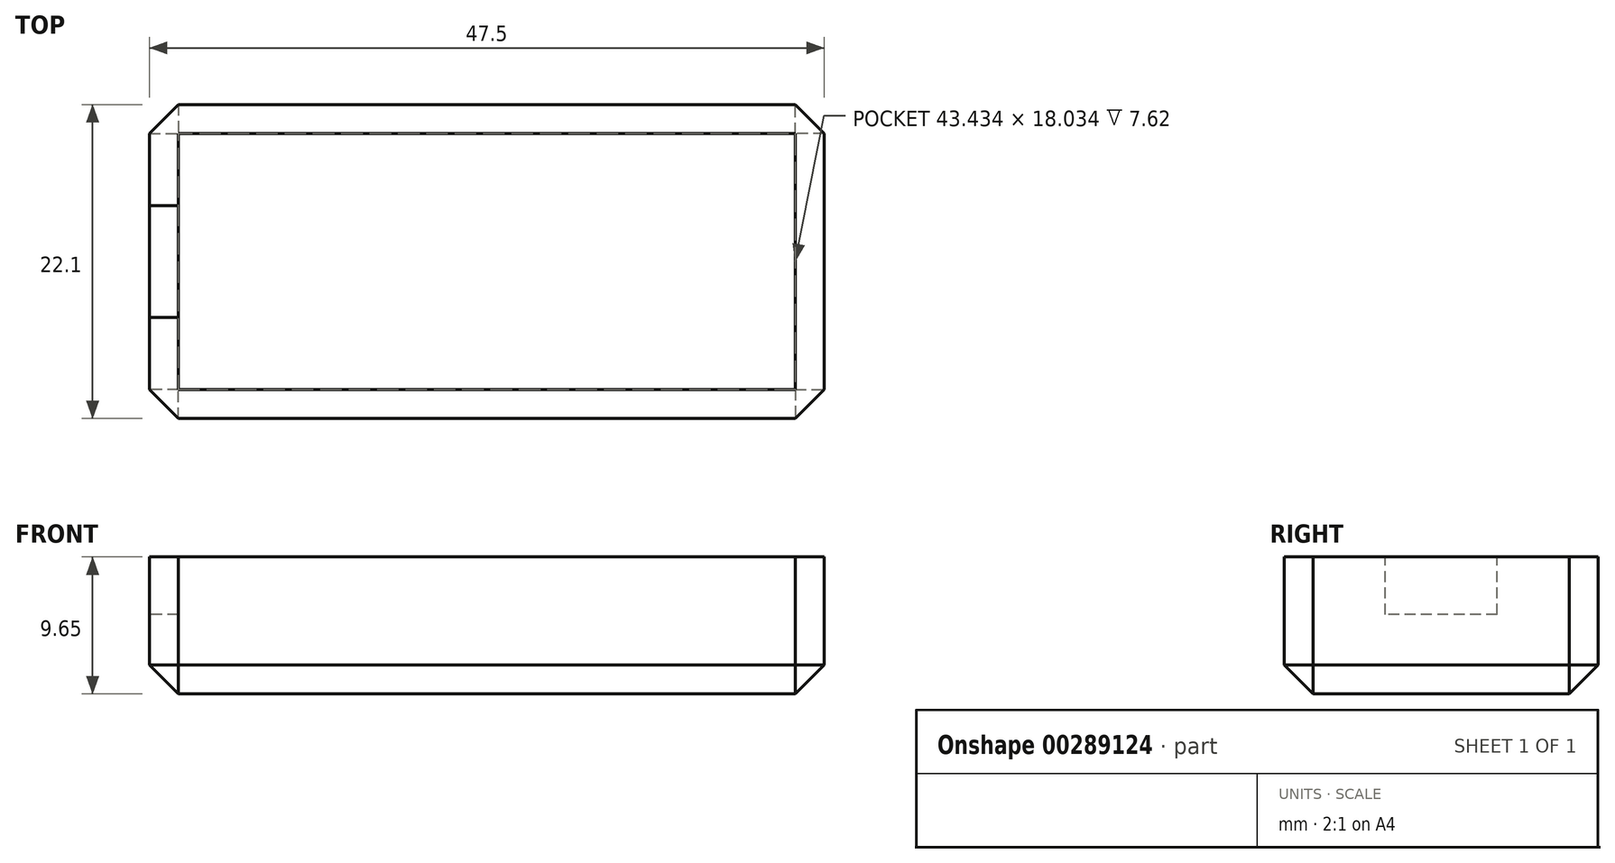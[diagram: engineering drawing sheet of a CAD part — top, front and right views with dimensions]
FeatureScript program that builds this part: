
annotation { "Feature Type Name" : "Feature", "Feature Type Description" : "" }
export const myFeature = defineFeature(function(context is Context, id is Id, definition is map)
    precondition{}
    {
        {
            var Q0;
            Q0=qCreatedBy(makeId("Top.planeOp"),FACE);
            var sketch = newSketch(context, id + "F0", { "sketchPlane" : qUnion([Q0])});
            skLineSegment(sketch, "E0.bottom", {"start": v(-23.75, 11.05) * mm, "end": v(23.75, 11.05) * mm});
            skLineSegment(sketch, "E0.top", {"start": v(-23.75, -11.05) * mm, "end": v(23.75, -11.05) * mm});
            skLineSegment(sketch, "E0.left", {"start": v(-23.75, 11.05) * mm, "end": v(-23.75, -11.05) * mm});
            skLineSegment(sketch, "E0.right", {"start": v(23.75, 11.05) * mm, "end": v(23.75, -11.05) * mm});
            skLineSegment(sketch, "E1", {"start": v(0, 0) * mm, "end": v(0, 11.05) * mm, "construction": true});
            skLineSegment(sketch, "E2", {"start": v(0, 0) * mm, "end": v(0, -11.05) * mm, "construction": true});
            skLineSegment(sketch, "E3", {"start": v(0, 0) * mm, "end": v(-23.75, 0) * mm, "construction": true});
            skPoint(sketch, "E3.endSnap0", {"position": v(-23.75, 0) * mm});
            skLineSegment(sketch, "E4", {"start": v(0, 0) * mm, "end": v(23.75, 0) * mm, "construction": true});
            skSolve(sketch);
        }
        {
            var Q0;
            Q0=makeQuery(id+"F0.imprint","IMPRINT",FACE,{"disambiguationData":[TD([[makeQuery(id+"F0.imprint","IMPRINT",EDGE,{"derivedFrom":sQuery(id+"F0.wireOp",EDGE,"E0.bottom")}),-1.0]])]});
            extrude(context, id + "F1", {"entities" : qUnion([Q0]), "depth" : 9.65 * mm});
        }
        {
            var Q0;
            Q0=makeQuery(id+"F1.opExtrude","CAP_FACE",FACE,{"disambiguationData":[OSD([sQuery(id+"F0.wireOp",EDGE,"E0.bottom"),sQuery(id+"F0.wireOp",EDGE,"E0.top"),sQuery(id+"F0.wireOp",EDGE,"E0.left"),sQuery(id+"F0.wireOp",EDGE,"E0.right")])],"isStart":false});
            var sketch = newSketch(context, id + "F2", { "sketchPlane" : qUnion([Q0])});
            skLineSegment(sketch, "E5.bottom", {"start": v(-21.72, 9.02) * mm, "end": v(21.72, 9.02) * mm});
            skLineSegment(sketch, "E5.top", {"start": v(-21.72, -9.02) * mm, "end": v(21.72, -9.02) * mm});
            skLineSegment(sketch, "E5.left", {"start": v(-21.72, 9.02) * mm, "end": v(-21.72, 4.29) * mm});
            skLineSegment(sketch, "E5.right", {"start": v(21.72, 9.02) * mm, "end": v(21.72, -9.02) * mm});
            skLineSegment(sketch, "E6", {"start": v(-21.72, 0) * mm, "end": v(-23.75, 0) * mm, "construction": true});
            skLineSegment(sketch, "E7", {"start": v(21.72, 0) * mm, "end": v(23.75, 0) * mm, "construction": true});
            skPoint(sketch, "E7.startSnap0", {"position": v(21.72, 0) * mm});
            skPoint(sketch, "E7.endSnap0", {"position": v(21.72, 0) * mm});
            skLineSegment(sketch, "E8", {"start": v(0, 9.02) * mm, "end": v(0, 11.05) * mm, "construction": true});
            skLineSegment(sketch, "E9", {"start": v(0, -9.02) * mm, "end": v(0, -11.05) * mm, "construction": true});
            skLineSegment(sketch, "E10.trimOffspring", {"start": v(-21.72, -4.29) * mm, "end": v(-21.72, -9.02) * mm});
            skLineSegment(sketch, "E11", {"start": v(-21.72, 4.29) * mm, "end": v(-21.72, -4.29) * mm});
            skSolve(sketch);
        }
        {
            var Q0;
            Q0=qSketchRegion(id+"F2",true);
            extrude(context, id + "F3", {"entities" : qUnion([Q0]), "operationType" : NewBodyOperationType.REMOVE, "oppositeDirection" : true, "depth" : 7.62 * mm});
        }
        {
            var Q0;
            Q0=makeQuery(id+"F1.opExtrude","CAP_EDGE",EDGE,{"disambiguationData":[OSD([sQuery(id+"F0.wireOp",EDGE,"E0.top")])],"isStart":true});
            var Q1;
            Q1=makeQuery(id+"F1.opExtrude","CAP_EDGE",EDGE,{"disambiguationData":[OSD([sQuery(id+"F0.wireOp",EDGE,"E0.right")])],"isStart":true});
            var Q2;
            Q2=makeQuery(id+"F1.opExtrude","SWEPT_EDGE",EDGE,{"disambiguationData":[OSD([sQuery(id+"F0.wireOp",EDGE,"E0.top"),sQuery(id+"F0.wireOp",EDGE,"E0.right")])]});
            var Q3;
            Q3=makeQuery(id+"F1.opExtrude","SWEPT_EDGE",EDGE,{"disambiguationData":[OSD([sQuery(id+"F0.wireOp",EDGE,"E0.bottom"),sQuery(id+"F0.wireOp",EDGE,"E0.right")])]});
            var Q4;
            Q4=makeQuery(id+"F1.opExtrude","CAP_EDGE",EDGE,{"disambiguationData":[OSD([sQuery(id+"F0.wireOp",EDGE,"E0.left")])],"isStart":true});
            var Q5;
            Q5=makeQuery(id+"F1.opExtrude","CAP_EDGE",EDGE,{"disambiguationData":[OSD([sQuery(id+"F0.wireOp",EDGE,"E0.bottom")])],"isStart":true});
            var Q6;
            Q6=makeQuery(id+"F1.opExtrude","SWEPT_EDGE",EDGE,{"disambiguationData":[OSD([sQuery(id+"F0.wireOp",EDGE,"E0.top"),sQuery(id+"F0.wireOp",EDGE,"E0.left")])]});
            var Q7;
            Q7=makeQuery(id+"F1.opExtrude","SWEPT_EDGE",EDGE,{"disambiguationData":[OSD([sQuery(id+"F0.wireOp",EDGE,"E0.bottom"),sQuery(id+"F0.wireOp",EDGE,"E0.left")])]});
            chamfer(context, id + "F4", {"entities" : qUnion([Q0, Q1, Q2, Q3, Q4, Q5, Q6, Q7]), "width" : 2.03 * mm, "tangentPropagation" : true});
        }
        {
            var Q0;
            Q0=makeQuery(id+"F1.opExtrude","CAP_FACE",FACE,{"disambiguationData":[OSD([sQuery(id+"F0.wireOp",EDGE,"E0.bottom"),sQuery(id+"F0.wireOp",EDGE,"E0.top"),sQuery(id+"F0.wireOp",EDGE,"E0.left"),sQuery(id+"F0.wireOp",EDGE,"E0.right")])],"isStart":false});
            var sketch = newSketch(context, id + "F5", { "sketchPlane" : qUnion([Q0])});
            skLineSegment(sketch, "E12.bottom", {"start": v(-21.72, 3.94) * mm, "end": v(-23.75, 3.94) * mm});
            skLineSegment(sketch, "E12.top", {"start": v(-21.72, -3.94) * mm, "end": v(-23.75, -3.94) * mm});
            skLineSegment(sketch, "E12.left", {"start": v(-21.72, 3.94) * mm, "end": v(-21.72, -3.94) * mm});
            skLineSegment(sketch, "E12.right", {"start": v(-23.75, 3.94) * mm, "end": v(-23.75, -3.94) * mm});
            skLineSegment(sketch, "E13", {"start": v(-22.73, -3.94) * mm, "end": v(-22.73, 0) * mm, "construction": true});
            skLineSegment(sketch, "E14", {"start": v(-22.73, 0) * mm, "end": v(-22.73, 3.94) * mm, "construction": true});
            skSolve(sketch);
        }
        {
            var Q0;
            Q0=makeQuery(id+"F5.imprint","IMPRINT",FACE,{"disambiguationData":[TD([[makeQuery(id+"F5.imprint","IMPRINT",EDGE,{"derivedFrom":sQuery(id+"F5.wireOp",EDGE,"E12.bottom")}),1.0]])]});
            extrude(context, id + "F6", {"entities" : qUnion([Q0]), "operationType" : NewBodyOperationType.REMOVE, "oppositeDirection" : true, "depth" : 4.06 * mm});
        }
    });
